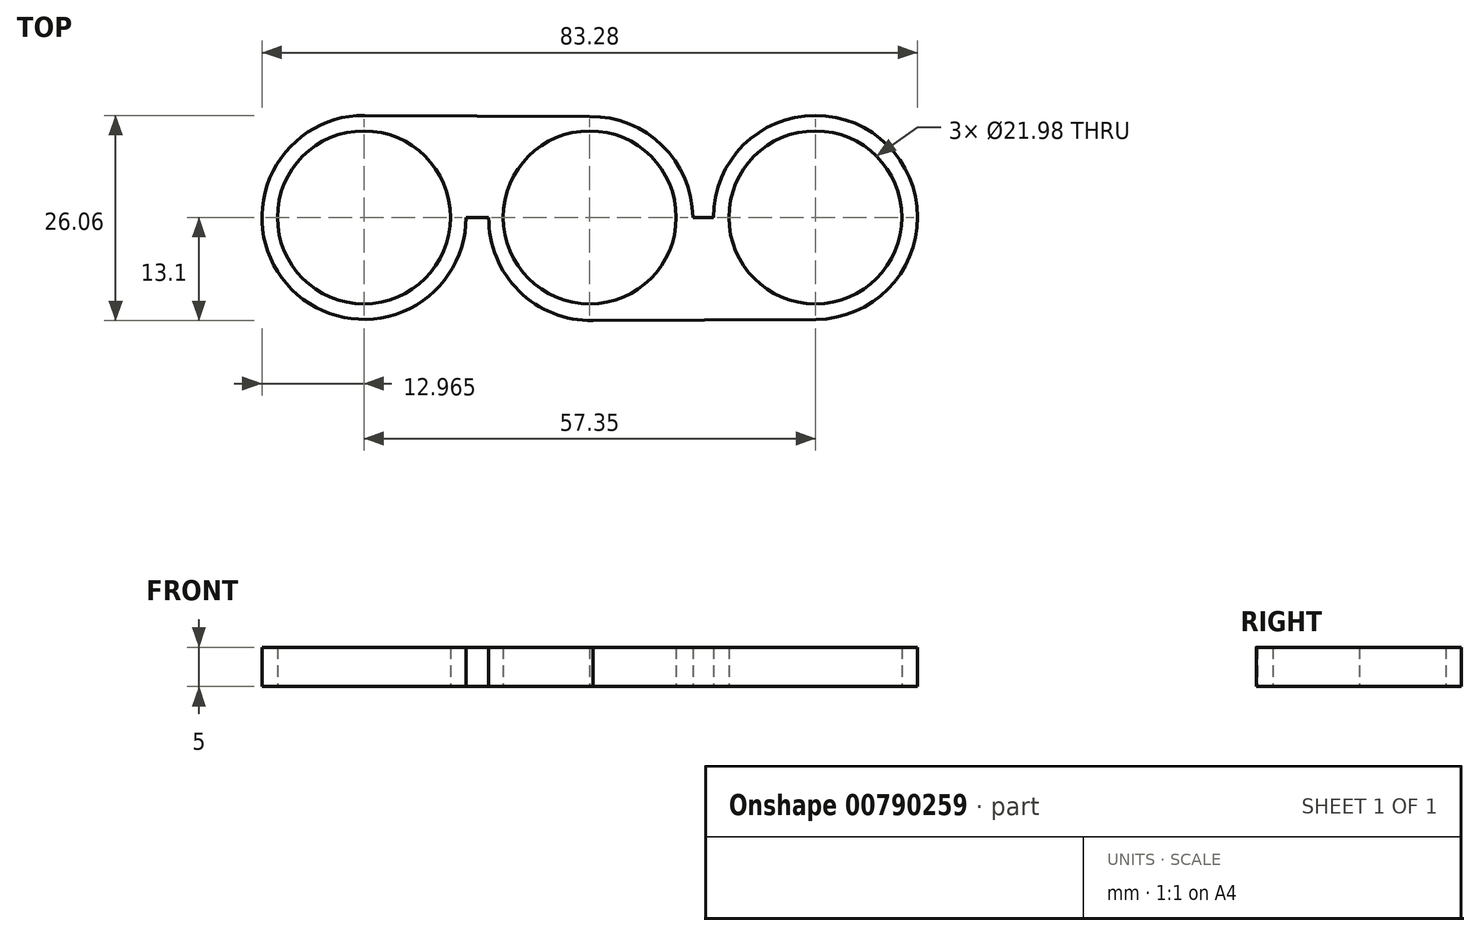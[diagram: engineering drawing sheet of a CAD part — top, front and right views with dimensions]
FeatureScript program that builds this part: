
annotation { "Feature Type Name" : "Feature", "Feature Type Description" : "" }
export const myFeature = defineFeature(function(context is Context, id is Id, definition is map)
    precondition{}
    {
        {
            var Q0;
            Q0=qCreatedBy(makeId("Top.planeOp"),FACE);
            var sketch = newSketch(context, id + "F0", { "sketchPlane" : qUnion([Q0])});
            skCircle(sketch, "E0", {"center": v(-28.67, 0) * mm, "radius": 12.96 * mm});
            skCircle(sketch, "E1", {"center": v(28.67, 0) * mm, "radius": 12.96 * mm});
            skCircle(sketch, "E2", {"center": v(0.14, -0.14) * mm, "radius": 12.96 * mm});
            skLineSegment(sketch, "E3", {"start": v(-15.71, 0) * mm, "end": v(-12.82, 0) * mm});
            skLineSegment(sketch, "E4", {"start": v(13.1, 0) * mm, "end": v(15.71, 0) * mm});
            skLineSegment(sketch, "E5", {"start": v(0, 12.82) * mm, "end": v(-28.61, 12.96) * mm});
            skLineSegment(sketch, "E6", {"start": v(0, -13.1) * mm, "end": v(28.74, -12.96) * mm});
            skCircle(sketch, "E7", {"center": v(0, 0) * mm, "radius": 10.99 * mm});
            skCircle(sketch, "E8", {"center": v(-28.67, 0) * mm, "radius": 10.99 * mm});
            skCircle(sketch, "E9", {"center": v(28.67, 0) * mm, "radius": 10.99 * mm});
            skSolve(sketch);
        }
        {
            var Q0;
            Q0 = qSketchRegion(id + "F0", true);
            extrude(context, id + "F1", {"entities" : qUnion([Q0]), "depth" : 5 * mm, "offsetDistance" : 25 * mm});
        }
    });
